# Revit family: Grundplatten Typ IV
name_source: partatom
category: HLS-Bauteile
revit_build: Autodesk Revit 2017 (Build: 20190507_1515(x64)
units: mm (PartAtom-declared; Revit-internal decimal feet)

## family parameters
Arbeitsebenenbasiert = Ja
Beim Laden mit Abzugskörper schneiden = Nein
Bemaßung runder Anschluss = Durchmesser verwenden
Gemeinsam genutzt = Ja
Immer vertikal = Nein
Raumberechnungspunkt = Nein
Teiletyp = Normal

## types (5) — shared parameters
Abmessung = 120 x 110 x 8 mm
Anzahl Befestigungsloch = 4
B = 110 mm  [stored 0.360892 ft]
B1 = 68 mm
Breite = 110 mm  [stored 0.360892 ft]
D = 14 mm  [stored 0.0459318 ft]
Fabrikat = MEFA
Firma = MEFA Befestigungs- und Montagesysteme GmbH
H = 23 mm  [stored 0.0754593 ft]
HGA = 15 mm  [stored 0.0492126 ft]
Kurztext1 = Grundplatte Typ IV
L = 120 mm  [stored 0.393701 ft]
L1 = 73 mm  [stored 0.239501 ft]
Langloch = 14x24 mm
Lochabstand längs = 73 mm  [stored 0.239501 ft]
Lochdurchmesser = 14 mm
Länge = 120 mm  [stored 0.393701 ft]
MD = 8 mm  [stored 0.0262467 ft]
Material = Stahl
Materialname = S235
Mengeneinheit = St
Oberflaeche = galvanisch verzinkt
Stärke = 8 mm  [stored 0.0262467 ft]
Vorgabe-Ansicht = 1219 mm
max. zul. Last hängend = 14.00 kN
vpe = 1 St
zero-valued in all types: Sicherheitsfaktor

## per-type parameters (varying)
| type | Anschluss | Artikelnummer | EAN | Gewicht | Gewicht pro Bauteil | Gewindeanschluss | Kurztext2 |
| Grundplatte Typ IV 120x110x8,0  M16 | M16 | 059055501 | 4250928415219 | 0.83 kg | 0.83 kg | 6kt-Mutter parametrik : Mutter M16 (4120522) | Anschluss M16 Platte 120x110x8 mm |
| Grundplatte Typ IV 120x110x8,0  1/2" | 1/2'' | 059055601 | 4250928415226 | 0.82 kg | 0.82 kg | Runde Gewindeanschlusse parametrik : Muffe 1/2´´ (0009865) | Anschluss 1/2'' Platte 120x110x8 mm |
| Grundplatte Typ IV 120x110x8,0  3/4" | 3/4'' | 059055701 | 4250928415233 | 0.83 kg | 0.83 kg | Runde Gewindeanschlusse parametrik : Schweißmuffe 3/4´´ (0009873) | Anschluss 3/4'' Platte 120x110x8 mm |
| Grundplatte Typ IV 120x110x8,0 1" | 1'' | 059055801 | 4250928415240 | 0.87 kg | 0.87 kg | Runde Gewindeanschlusse parametrik : Muffe 1´´ (0009881) | Anschluss 1'' Platte 120x110x8 mm |
| Grundplatte Typ IV 120x110x8,0  1 1/4" | 1 1/4'' | 059055901 | 4250928415257 | 0.90 kg | 0.90 kg | Runde Gewindeanschlusse parametrik : Muffe 1 1/4´´ (0009898) | Anschluss 1 1/4'' Platte 120x110x8 mm |

note: [stored X ft] marks values corroborated as IEEE doubles in the binary element streams (Revit-internal decimal feet)

## geometry (parser evidence)
native form markers: Sweep x8
no freeform markers — native parametric forms only
